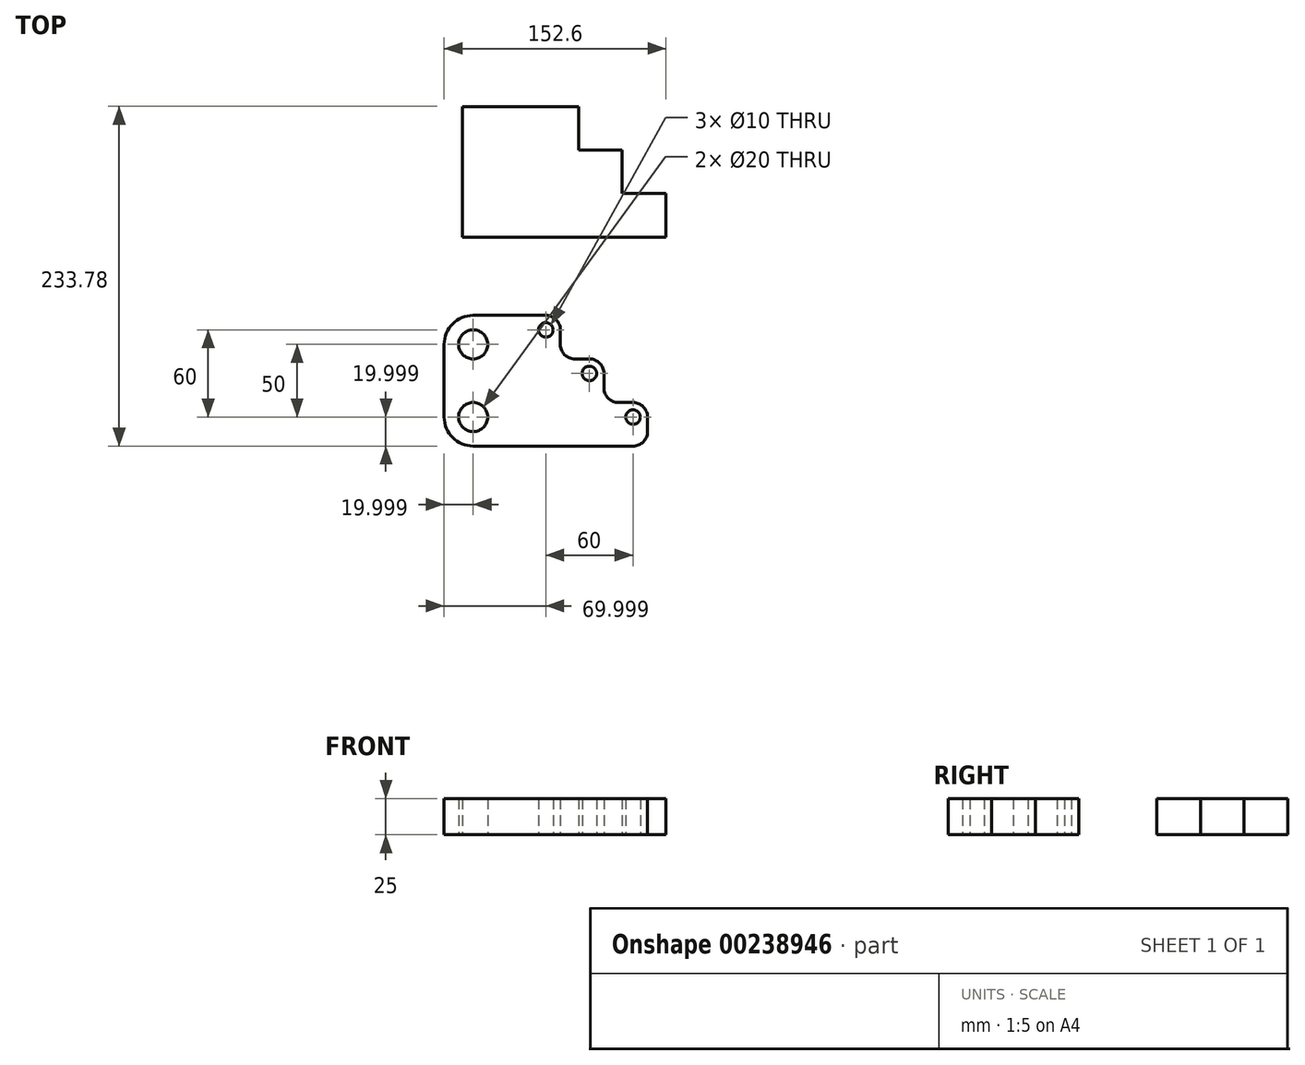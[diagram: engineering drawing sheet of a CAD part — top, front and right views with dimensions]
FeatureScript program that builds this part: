
annotation { "Feature Type Name" : "Feature", "Feature Type Description" : "" }
export const myFeature = defineFeature(function(context is Context, id is Id, definition is map)
    precondition{}
    {
        {
            var Q0;
            Q0=qCreatedBy(makeId("Top.planeOp"),FACE);
            var sketch = newSketch(context, id + "F0", { "sketchPlane" : qUnion([Q0])});
            skLineSegment(sketch, "E0", {"start": v(-40.41, 3.37) * mm, "end": v(99.59, 3.37) * mm});
            skLineSegment(sketch, "E1", {"start": v(99.59, 3.37) * mm, "end": v(99.59, 33.37) * mm});
            skLineSegment(sketch, "E2", {"start": v(99.59, 33.37) * mm, "end": v(69.59, 33.37) * mm});
            skLineSegment(sketch, "E3", {"start": v(69.59, 33.37) * mm, "end": v(69.59, 63.37) * mm});
            skLineSegment(sketch, "E4", {"start": v(69.59, 63.37) * mm, "end": v(39.59, 63.37) * mm});
            skLineSegment(sketch, "E5", {"start": v(39.59, 63.37) * mm, "end": v(39.59, 93.37) * mm});
            skLineSegment(sketch, "E6", {"start": v(39.59, 93.37) * mm, "end": v(-40.41, 93.37) * mm});
            skLineSegment(sketch, "E7", {"start": v(-40.41, 93.37) * mm, "end": v(-40.41, 3.37) * mm});
            skLineSegment(sketch, "E8", {"start": v(-53.01, -70.41) * mm, "end": v(-53.01, -120.41) * mm});
            skLineSegment(sketch, "E9", {"start": v(-33.01, -140.41) * mm, "end": v(76.99, -140.41) * mm});
            skLineSegment(sketch, "E10", {"start": v(86.99, -130.41) * mm, "end": v(86.99, -120.41) * mm});
            skLineSegment(sketch, "E11", {"start": v(76.99, -110.41) * mm, "end": v(66.99, -110.41) * mm});
            skLineSegment(sketch, "E12", {"start": v(56.99, -100.41) * mm, "end": v(56.99, -90.41) * mm});
            skLineSegment(sketch, "E13", {"start": v(46.99, -80.41) * mm, "end": v(36.99, -80.41) * mm});
            skLineSegment(sketch, "E14", {"start": v(26.99, -70.41) * mm, "end": v(26.99, -60.41) * mm});
            skLineSegment(sketch, "E15", {"start": v(16.99, -50.41) * mm, "end": v(-33.01, -50.41) * mm});
            skPoint(sketch, "E16.visualSharp", {"position": v(-53.01, -140.41) * mm});
            skArc(sketch, "E16.filletArc", {"start": v(-53.01, -120.41) * mm, "mid": v(-47.15, -134.55) * mm, "end": v(-33.01, -140.41) * mm});
            skPoint(sketch, "E17.visualSharp", {"position": v(-53.01, -50.41) * mm});
            skArc(sketch, "E17.filletArc", {"start": v(-33.01, -50.41) * mm, "mid": v(-47.15, -56.27) * mm, "end": v(-53.01, -70.41) * mm});
            skPoint(sketch, "E18.visualSharp", {"position": v(86.99, -140.41) * mm});
            skArc(sketch, "E18.filletArc", {"start": v(76.99, -140.41) * mm, "mid": v(84.06, -137.48) * mm, "end": v(86.99, -130.41) * mm});
            skPoint(sketch, "E19.visualSharp", {"position": v(86.99, -110.41) * mm});
            skArc(sketch, "E19.filletArc", {"start": v(86.99, -120.41) * mm, "mid": v(84.06, -113.34) * mm, "end": v(76.99, -110.41) * mm});
            skPoint(sketch, "E20.visualSharp", {"position": v(56.99, -110.41) * mm});
            skArc(sketch, "E20.filletArc", {"start": v(56.99, -100.41) * mm, "mid": v(59.92, -107.48) * mm, "end": v(66.99, -110.41) * mm});
            skPoint(sketch, "E21.visualSharp", {"position": v(56.99, -80.41) * mm});
            skArc(sketch, "E21.filletArc", {"start": v(56.99, -90.41) * mm, "mid": v(54.06, -83.34) * mm, "end": v(46.99, -80.41) * mm});
            skPoint(sketch, "E22.visualSharp", {"position": v(26.99, -80.41) * mm});
            skArc(sketch, "E22.filletArc", {"start": v(26.99, -70.41) * mm, "mid": v(29.92, -77.48) * mm, "end": v(36.99, -80.41) * mm});
            skPoint(sketch, "E23.visualSharp", {"position": v(26.99, -50.41) * mm});
            skArc(sketch, "E23.filletArc", {"start": v(26.99, -60.41) * mm, "mid": v(24.06, -53.34) * mm, "end": v(16.99, -50.41) * mm});
            skCircle(sketch, "E24", {"center": v(16.99, -60.41) * mm, "radius": 5 * mm});
            skCircle(sketch, "E25", {"center": v(46.99, -90.41) * mm, "radius": 5 * mm});
            skCircle(sketch, "E26", {"center": v(76.99, -120.41) * mm, "radius": 5 * mm});
            skCircle(sketch, "E27", {"center": v(-33.01, -120.41) * mm, "radius": 10 * mm});
            skCircle(sketch, "E28", {"center": v(-33.01, -70.41) * mm, "radius": 10 * mm});
            skSolve(sketch);
        }
        {
            var Q0;
            Q0 = qSketchRegion(id + "F0", true);
            extrude(context, id + "F1", {"entities" : qUnion([Q0]), "depth" : 25 * mm});
        }
    });
